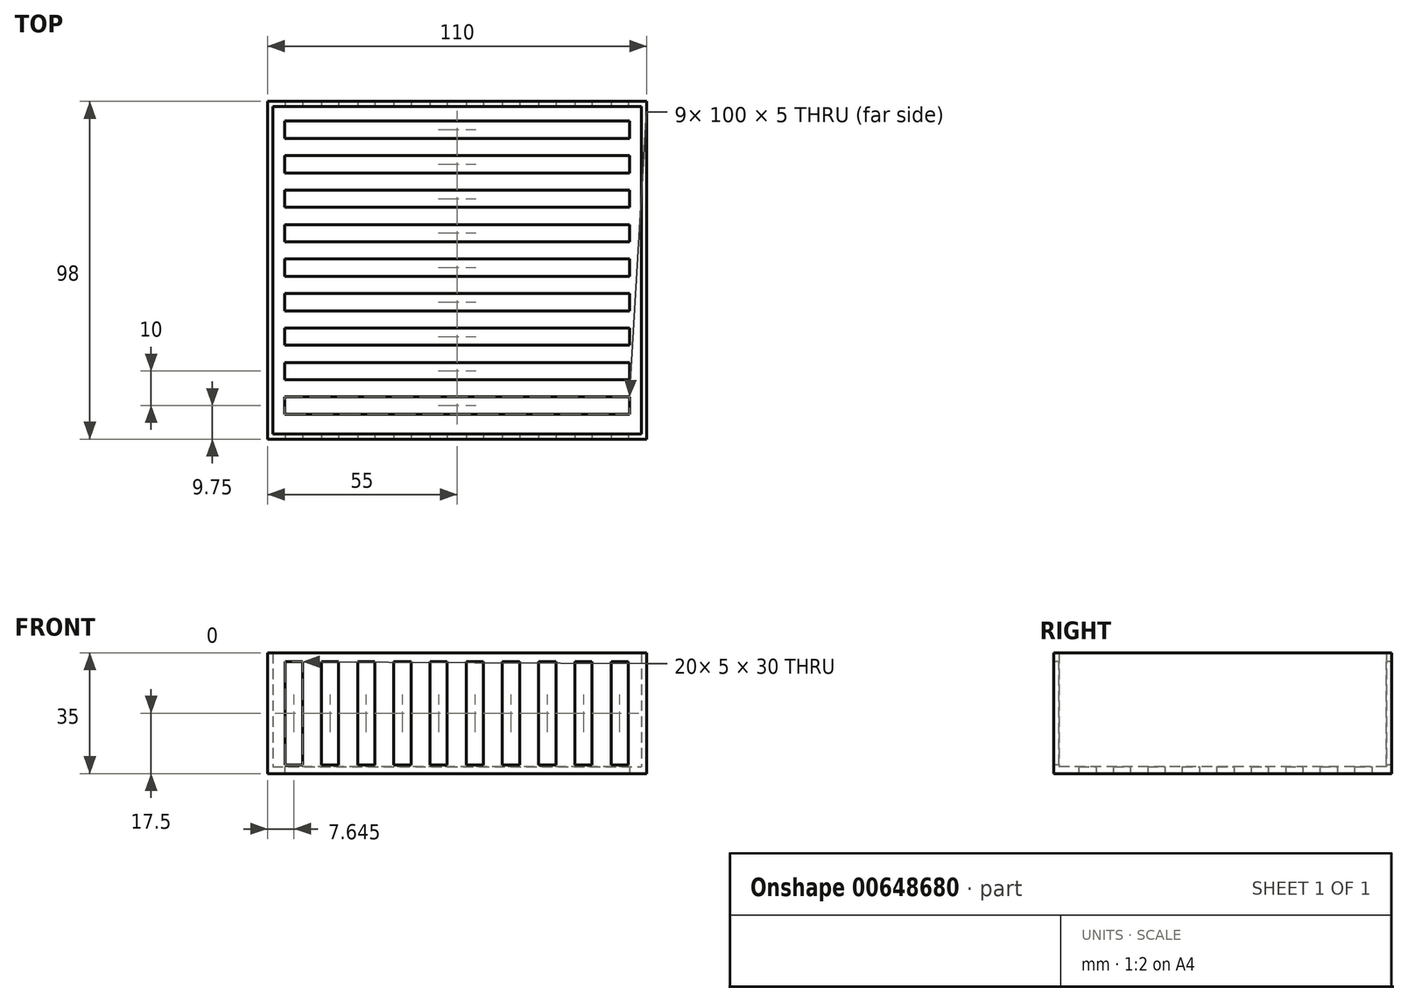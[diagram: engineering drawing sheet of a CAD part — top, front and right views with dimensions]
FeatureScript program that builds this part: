
annotation { "Feature Type Name" : "Feature", "Feature Type Description" : "" }
export const myFeature = defineFeature(function(context is Context, id is Id, definition is map)
    precondition{}
    {
        {
            var Q0;
            Q0=qCreatedBy(makeId("Top.planeOp"),FACE);
            var sketch = newSketch(context, id + "F0", { "sketchPlane" : qUnion([Q0])});
            skLineSegment(sketch, "E0.bottom", {"start": v(55, -49) * mm, "end": v(-55, -49) * mm});
            skLineSegment(sketch, "E0.top", {"start": v(55, 49) * mm, "end": v(-55, 49) * mm});
            skLineSegment(sketch, "E0.left", {"start": v(55, -49) * mm, "end": v(55, 49) * mm});
            skLineSegment(sketch, "E0.right", {"start": v(-55, -49) * mm, "end": v(-55, 49) * mm});
            skPoint(sketch, "E0.middle", {"position": v(0, 0) * mm});
            skLineSegment(sketch, "E1.0", {"start": v(53.5, 47.5) * mm, "end": v(-53.5, 47.5) * mm});
            skLineSegment(sketch, "E1.1", {"start": v(53.5, -47.5) * mm, "end": v(53.5, 47.5) * mm});
            skLineSegment(sketch, "E1.2", {"start": v(53.5, -47.5) * mm, "end": v(-53.5, -47.5) * mm});
            skLineSegment(sketch, "E1.3", {"start": v(-53.5, -47.5) * mm, "end": v(-53.5, 47.5) * mm});
            skLineSegment(sketch, "E2.bottom", {"start": v(50, 38.25) * mm, "end": v(-50, 38.25) * mm});
            skLineSegment(sketch, "E2.top", {"start": v(50, 43.25) * mm, "end": v(-50, 43.25) * mm});
            skLineSegment(sketch, "E2.left", {"start": v(50, 38.25) * mm, "end": v(50, 43.25) * mm});
            skLineSegment(sketch, "E2.right", {"start": v(-50, 38.25) * mm, "end": v(-50, 43.25) * mm});
            skPoint(sketch, "E2.middle", {"position": v(0, 40.75) * mm});
            skLineSegment(sketch, "E3.0.1.0", {"start": v(50, 28.25) * mm, "end": v(-50, 28.25) * mm});
            skLineSegment(sketch, "E3.0.1.1", {"start": v(50, 33.25) * mm, "end": v(-50, 33.25) * mm});
            skLineSegment(sketch, "E3.0.1.2", {"start": v(50, 28.25) * mm, "end": v(50, 33.25) * mm});
            skLineSegment(sketch, "E3.0.1.3", {"start": v(-50, 28.25) * mm, "end": v(-50, 33.25) * mm});
            skPoint(sketch, "E3.0.1.4", {"position": v(0, 30.75) * mm});
            skLineSegment(sketch, "E3.0.2.0", {"start": v(50, 18.25) * mm, "end": v(-50, 18.25) * mm});
            skLineSegment(sketch, "E3.0.2.1", {"start": v(50, 23.25) * mm, "end": v(-50, 23.25) * mm});
            skLineSegment(sketch, "E3.0.2.2", {"start": v(50, 18.25) * mm, "end": v(50, 23.25) * mm});
            skLineSegment(sketch, "E3.0.2.3", {"start": v(-50, 18.25) * mm, "end": v(-50, 23.25) * mm});
            skPoint(sketch, "E3.0.2.4", {"position": v(0, 20.75) * mm});
            skLineSegment(sketch, "E3.0.3.0", {"start": v(50, 8.25) * mm, "end": v(-50, 8.25) * mm});
            skLineSegment(sketch, "E3.0.3.1", {"start": v(50, 13.25) * mm, "end": v(-50, 13.25) * mm});
            skLineSegment(sketch, "E3.0.3.2", {"start": v(50, 8.25) * mm, "end": v(50, 13.25) * mm});
            skLineSegment(sketch, "E3.0.3.3", {"start": v(-50, 8.25) * mm, "end": v(-50, 13.25) * mm});
            skPoint(sketch, "E3.0.3.4", {"position": v(0, 10.75) * mm});
            skLineSegment(sketch, "E3.0.4.0", {"start": v(50, -1.75) * mm, "end": v(-50, -1.75) * mm});
            skLineSegment(sketch, "E3.0.4.1", {"start": v(50, 3.25) * mm, "end": v(-50, 3.25) * mm});
            skLineSegment(sketch, "E3.0.4.2", {"start": v(50, -1.75) * mm, "end": v(50, 3.25) * mm});
            skLineSegment(sketch, "E3.0.4.3", {"start": v(-50, -1.75) * mm, "end": v(-50, 3.25) * mm});
            skPoint(sketch, "E3.0.4.4", {"position": v(0, 0.75) * mm});
            skLineSegment(sketch, "E3.0.5.0", {"start": v(50, -11.75) * mm, "end": v(-50, -11.75) * mm});
            skLineSegment(sketch, "E3.0.5.1", {"start": v(50, -6.75) * mm, "end": v(-50, -6.75) * mm});
            skLineSegment(sketch, "E3.0.5.2", {"start": v(50, -11.75) * mm, "end": v(50, -6.75) * mm});
            skLineSegment(sketch, "E3.0.5.3", {"start": v(-50, -11.75) * mm, "end": v(-50, -6.75) * mm});
            skPoint(sketch, "E3.0.5.4", {"position": v(0, -9.25) * mm});
            skLineSegment(sketch, "E3.0.6.0", {"start": v(50, -21.75) * mm, "end": v(-50, -21.75) * mm});
            skLineSegment(sketch, "E3.0.6.1", {"start": v(50, -16.75) * mm, "end": v(-50, -16.75) * mm});
            skLineSegment(sketch, "E3.0.6.2", {"start": v(50, -21.75) * mm, "end": v(50, -16.75) * mm});
            skLineSegment(sketch, "E3.0.6.3", {"start": v(-50, -21.75) * mm, "end": v(-50, -16.75) * mm});
            skPoint(sketch, "E3.0.6.4", {"position": v(0, -19.25) * mm});
            skLineSegment(sketch, "E3.0.7.0", {"start": v(50, -31.75) * mm, "end": v(-50, -31.75) * mm});
            skLineSegment(sketch, "E3.0.7.1", {"start": v(50, -26.75) * mm, "end": v(-50, -26.75) * mm});
            skLineSegment(sketch, "E3.0.7.2", {"start": v(50, -31.75) * mm, "end": v(50, -26.75) * mm});
            skLineSegment(sketch, "E3.0.7.3", {"start": v(-50, -31.75) * mm, "end": v(-50, -26.75) * mm});
            skPoint(sketch, "E3.0.7.4", {"position": v(0, -29.25) * mm});
            skLineSegment(sketch, "E3.0.8.0", {"start": v(50, -41.75) * mm, "end": v(-50, -41.75) * mm});
            skLineSegment(sketch, "E3.0.8.1", {"start": v(50, -36.75) * mm, "end": v(-50, -36.75) * mm});
            skLineSegment(sketch, "E3.0.8.2", {"start": v(50, -41.75) * mm, "end": v(50, -36.75) * mm});
            skLineSegment(sketch, "E3.0.8.3", {"start": v(-50, -41.75) * mm, "end": v(-50, -36.75) * mm});
            skPoint(sketch, "E3.0.8.4", {"position": v(0, -39.25) * mm});
            skLineSegment(sketch, "E3.direction1", {"start": v(-50, 38.25) * mm, "end": v(-25, 38.25) * mm, "construction": true});
            skLineSegment(sketch, "E3.direction2", {"start": v(-50, 38.25) * mm, "end": v(-50, 28.25) * mm, "construction": true});
            skSolve(sketch);
        }
        {
            var Q0;
            Q0=makeQuery(id+"F0.imprint","IMPRINT",FACE,{"disambiguationData":[TD([[makeQuery(id+"F0.imprint","IMPRINT",EDGE,{"derivedFrom":sQuery(id+"F0.wireOp",EDGE,"E1.0")}),1.0]])]});
            var Q1;
            Q1=makeQuery(id+"F0.imprint","IMPRINT",FACE,{"disambiguationData":[TD([[makeQuery(id+"F0.imprint","IMPRINT",EDGE,{"derivedFrom":sQuery(id+"F0.wireOp",EDGE,"E0.bottom")}),-1.0]])]});
            extrude(context, id + "F1", {"entities" : qUnion([Q0, Q1]), "depth" : 2 * mm, "offsetDistance" : 25 * mm});
        }
        {
            var Q0;
            Q0=makeQuery(id+"F0.imprint","IMPRINT",FACE,{"disambiguationData":[TD([[makeQuery(id+"F0.imprint","IMPRINT",EDGE,{"derivedFrom":sQuery(id+"F0.wireOp",EDGE,"E0.bottom")}),-1.0]])]});
            extrude(context, id + "F2", {"entities" : qUnion([Q0]), "operationType" : NewBodyOperationType.ADD, "depth" : 35 * mm, "offsetDistance" : 25 * mm});
        }
        {
            var Q0;
            {var subQ0=sQuery(id+"F0.wireOp",EDGE,"E0.bottom");Q0=makeQuery(id+"F2.boolean.opBoolean","MERGE",FACE,{"derivedFrom":[makeQuery(id+"F1.opExtrude","SWEPT_FACE",FACE,{"disambiguationData":[OSD([subQ0])]}),makeQuery(id+"F2.opExtrude","SWEPT_FACE",FACE,{"disambiguationData":[OSD([subQ0])]})]});}
            var sketch = newSketch(context, id + "F3", { "sketchPlane" : qUnion([Q0])});
            skLineSegment(sketch, "E4.bottom", {"start": v(-44.85, 2.5) * mm, "end": v(-49.85, 2.5) * mm});
            skLineSegment(sketch, "E4.top", {"start": v(-44.85, 32.5) * mm, "end": v(-49.85, 32.5) * mm});
            skLineSegment(sketch, "E4.left", {"start": v(-44.85, 2.5) * mm, "end": v(-44.85, 32.5) * mm});
            skLineSegment(sketch, "E4.right", {"start": v(-49.85, 2.5) * mm, "end": v(-49.85, 32.5) * mm});
            skPoint(sketch, "E4.middle", {"position": v(-47.35, 17.5) * mm});
            skPoint(sketch, "E4.middle.positionSnap0", {"position": v(-55, 17.5) * mm});
            skPoint(sketch, "E4.centerSnap0", {"position": v(-55, 17.5) * mm});
            skPoint(sketch, "E5.1.0.0", {"position": v(-36.85, 17.5) * mm});
            skLineSegment(sketch, "E5.1.0.1", {"start": v(-34.35, 2.5) * mm, "end": v(-39.35, 2.5) * mm});
            skLineSegment(sketch, "E5.1.0.2", {"start": v(-34.35, 32.5) * mm, "end": v(-39.35, 32.5) * mm});
            skLineSegment(sketch, "E5.1.0.3", {"start": v(-34.35, 2.5) * mm, "end": v(-34.35, 32.5) * mm});
            skLineSegment(sketch, "E5.1.0.4", {"start": v(-39.35, 2.5) * mm, "end": v(-39.35, 32.5) * mm});
            skPoint(sketch, "E5.2.0.0", {"position": v(-26.35, 17.5) * mm});
            skLineSegment(sketch, "E5.2.0.1", {"start": v(-23.85, 2.5) * mm, "end": v(-28.85, 2.5) * mm});
            skLineSegment(sketch, "E5.2.0.2", {"start": v(-23.85, 32.5) * mm, "end": v(-28.85, 32.5) * mm});
            skLineSegment(sketch, "E5.2.0.3", {"start": v(-23.85, 2.5) * mm, "end": v(-23.85, 32.5) * mm});
            skLineSegment(sketch, "E5.2.0.4", {"start": v(-28.85, 2.5) * mm, "end": v(-28.85, 32.5) * mm});
            skPoint(sketch, "E5.3.0.0", {"position": v(-15.85, 17.5) * mm});
            skLineSegment(sketch, "E5.3.0.1", {"start": v(-13.35, 2.5) * mm, "end": v(-18.35, 2.5) * mm});
            skLineSegment(sketch, "E5.3.0.2", {"start": v(-13.35, 32.5) * mm, "end": v(-18.35, 32.5) * mm});
            skLineSegment(sketch, "E5.3.0.3", {"start": v(-13.35, 2.5) * mm, "end": v(-13.35, 32.5) * mm});
            skLineSegment(sketch, "E5.3.0.4", {"start": v(-18.35, 2.5) * mm, "end": v(-18.35, 32.5) * mm});
            skPoint(sketch, "E5.4.0.0", {"position": v(-5.35, 17.5) * mm});
            skLineSegment(sketch, "E5.4.0.1", {"start": v(-2.85, 2.5) * mm, "end": v(-7.85, 2.5) * mm});
            skLineSegment(sketch, "E5.4.0.2", {"start": v(-2.85, 32.5) * mm, "end": v(-7.85, 32.5) * mm});
            skLineSegment(sketch, "E5.4.0.3", {"start": v(-2.85, 2.5) * mm, "end": v(-2.85, 32.5) * mm});
            skLineSegment(sketch, "E5.4.0.4", {"start": v(-7.85, 2.5) * mm, "end": v(-7.85, 32.5) * mm});
            skPoint(sketch, "E5.5.0.0", {"position": v(5.15, 17.5) * mm});
            skLineSegment(sketch, "E5.5.0.1", {"start": v(7.65, 2.5) * mm, "end": v(2.65, 2.5) * mm});
            skLineSegment(sketch, "E5.5.0.2", {"start": v(7.65, 32.5) * mm, "end": v(2.65, 32.5) * mm});
            skLineSegment(sketch, "E5.5.0.3", {"start": v(7.65, 2.5) * mm, "end": v(7.65, 32.5) * mm});
            skLineSegment(sketch, "E5.5.0.4", {"start": v(2.65, 2.5) * mm, "end": v(2.65, 32.5) * mm});
            skPoint(sketch, "E5.6.0.0", {"position": v(15.65, 17.5) * mm});
            skLineSegment(sketch, "E5.6.0.1", {"start": v(18.15, 2.5) * mm, "end": v(13.15, 2.5) * mm});
            skLineSegment(sketch, "E5.6.0.2", {"start": v(18.15, 32.5) * mm, "end": v(13.15, 32.5) * mm});
            skLineSegment(sketch, "E5.6.0.3", {"start": v(18.15, 2.5) * mm, "end": v(18.15, 32.5) * mm});
            skLineSegment(sketch, "E5.6.0.4", {"start": v(13.15, 2.5) * mm, "end": v(13.15, 32.5) * mm});
            skPoint(sketch, "E5.7.0.0", {"position": v(26.15, 17.5) * mm});
            skLineSegment(sketch, "E5.7.0.1", {"start": v(28.65, 2.5) * mm, "end": v(23.65, 2.5) * mm});
            skLineSegment(sketch, "E5.7.0.2", {"start": v(28.65, 32.5) * mm, "end": v(23.65, 32.5) * mm});
            skLineSegment(sketch, "E5.7.0.3", {"start": v(28.65, 2.5) * mm, "end": v(28.65, 32.5) * mm});
            skLineSegment(sketch, "E5.7.0.4", {"start": v(23.65, 2.5) * mm, "end": v(23.65, 32.5) * mm});
            skPoint(sketch, "E5.8.0.0", {"position": v(36.65, 17.5) * mm});
            skLineSegment(sketch, "E5.8.0.1", {"start": v(39.15, 2.5) * mm, "end": v(34.15, 2.5) * mm});
            skLineSegment(sketch, "E5.8.0.2", {"start": v(39.15, 32.5) * mm, "end": v(34.15, 32.5) * mm});
            skLineSegment(sketch, "E5.8.0.3", {"start": v(39.15, 2.5) * mm, "end": v(39.15, 32.5) * mm});
            skLineSegment(sketch, "E5.8.0.4", {"start": v(34.15, 2.5) * mm, "end": v(34.15, 32.5) * mm});
            skPoint(sketch, "E5.9.0.0", {"position": v(47.15, 17.5) * mm});
            skLineSegment(sketch, "E5.9.0.1", {"start": v(49.65, 2.5) * mm, "end": v(44.65, 2.5) * mm});
            skLineSegment(sketch, "E5.9.0.2", {"start": v(49.65, 32.5) * mm, "end": v(44.65, 32.5) * mm});
            skLineSegment(sketch, "E5.9.0.3", {"start": v(49.65, 2.5) * mm, "end": v(49.65, 32.5) * mm});
            skLineSegment(sketch, "E5.9.0.4", {"start": v(44.65, 2.5) * mm, "end": v(44.65, 32.5) * mm});
            skLineSegment(sketch, "E5.direction1", {"start": v(-49.85, 2.5) * mm, "end": v(-39.35, 2.5) * mm, "construction": true});
            skSolve(sketch);
        }
        {
            var Q0;
            Q0=makeQuery(id+"F3.imprint","IMPRINT",FACE,{"disambiguationData":[TD([[makeQuery(id+"F3.imprint","IMPRINT",EDGE,{"derivedFrom":sQuery(id+"F3.wireOp",EDGE,"E5.1.0.1")}),-1.0]])]});
            var Q1;
            Q1=makeQuery(id+"F3.imprint","IMPRINT",FACE,{"disambiguationData":[TD([[makeQuery(id+"F3.imprint","IMPRINT",EDGE,{"derivedFrom":sQuery(id+"F3.wireOp",EDGE,"E4.bottom")}),-1.0]])]});
            var Q2;
            Q2=makeQuery(id+"F3.imprint","IMPRINT",FACE,{"disambiguationData":[TD([[makeQuery(id+"F3.imprint","IMPRINT",EDGE,{"derivedFrom":sQuery(id+"F3.wireOp",EDGE,"E5.2.0.1")}),-1.0]])]});
            var Q3;
            Q3=makeQuery(id+"F3.imprint","IMPRINT",FACE,{"disambiguationData":[TD([[makeQuery(id+"F3.imprint","IMPRINT",EDGE,{"derivedFrom":sQuery(id+"F3.wireOp",EDGE,"E5.3.0.1")}),-1.0]])]});
            var Q4;
            Q4=makeQuery(id+"F3.imprint","IMPRINT",FACE,{"disambiguationData":[TD([[makeQuery(id+"F3.imprint","IMPRINT",EDGE,{"derivedFrom":sQuery(id+"F3.wireOp",EDGE,"E5.4.0.1")}),-1.0]])]});
            var Q5;
            Q5=makeQuery(id+"F3.imprint","IMPRINT",FACE,{"disambiguationData":[TD([[makeQuery(id+"F3.imprint","IMPRINT",EDGE,{"derivedFrom":sQuery(id+"F3.wireOp",EDGE,"E5.5.0.1")}),-1.0]])]});
            var Q6;
            Q6=makeQuery(id+"F3.imprint","IMPRINT",FACE,{"disambiguationData":[TD([[makeQuery(id+"F3.imprint","IMPRINT",EDGE,{"derivedFrom":sQuery(id+"F3.wireOp",EDGE,"E5.6.0.1")}),-1.0]])]});
            var Q7;
            Q7=makeQuery(id+"F3.imprint","IMPRINT",FACE,{"disambiguationData":[TD([[makeQuery(id+"F3.imprint","IMPRINT",EDGE,{"derivedFrom":sQuery(id+"F3.wireOp",EDGE,"E5.7.0.1")}),-1.0]])]});
            var Q8;
            Q8=makeQuery(id+"F3.imprint","IMPRINT",FACE,{"disambiguationData":[TD([[makeQuery(id+"F3.imprint","IMPRINT",EDGE,{"derivedFrom":sQuery(id+"F3.wireOp",EDGE,"E5.8.0.1")}),-1.0]])]});
            var Q9;
            Q9=makeQuery(id+"F3.imprint","IMPRINT",FACE,{"disambiguationData":[TD([[makeQuery(id+"F3.imprint","IMPRINT",EDGE,{"derivedFrom":sQuery(id+"F3.wireOp",EDGE,"E5.9.0.1")}),-1.0]])]});
            extrude(context, id + "F4", {"entities" : qUnion([Q0, Q1, Q2, Q3, Q4, Q5, Q6, Q7, Q8, Q9]), "operationType" : NewBodyOperationType.REMOVE, "oppositeDirection" : true, "depth" : 150 * mm, "offsetDistance" : 25 * mm});
        }
    });
